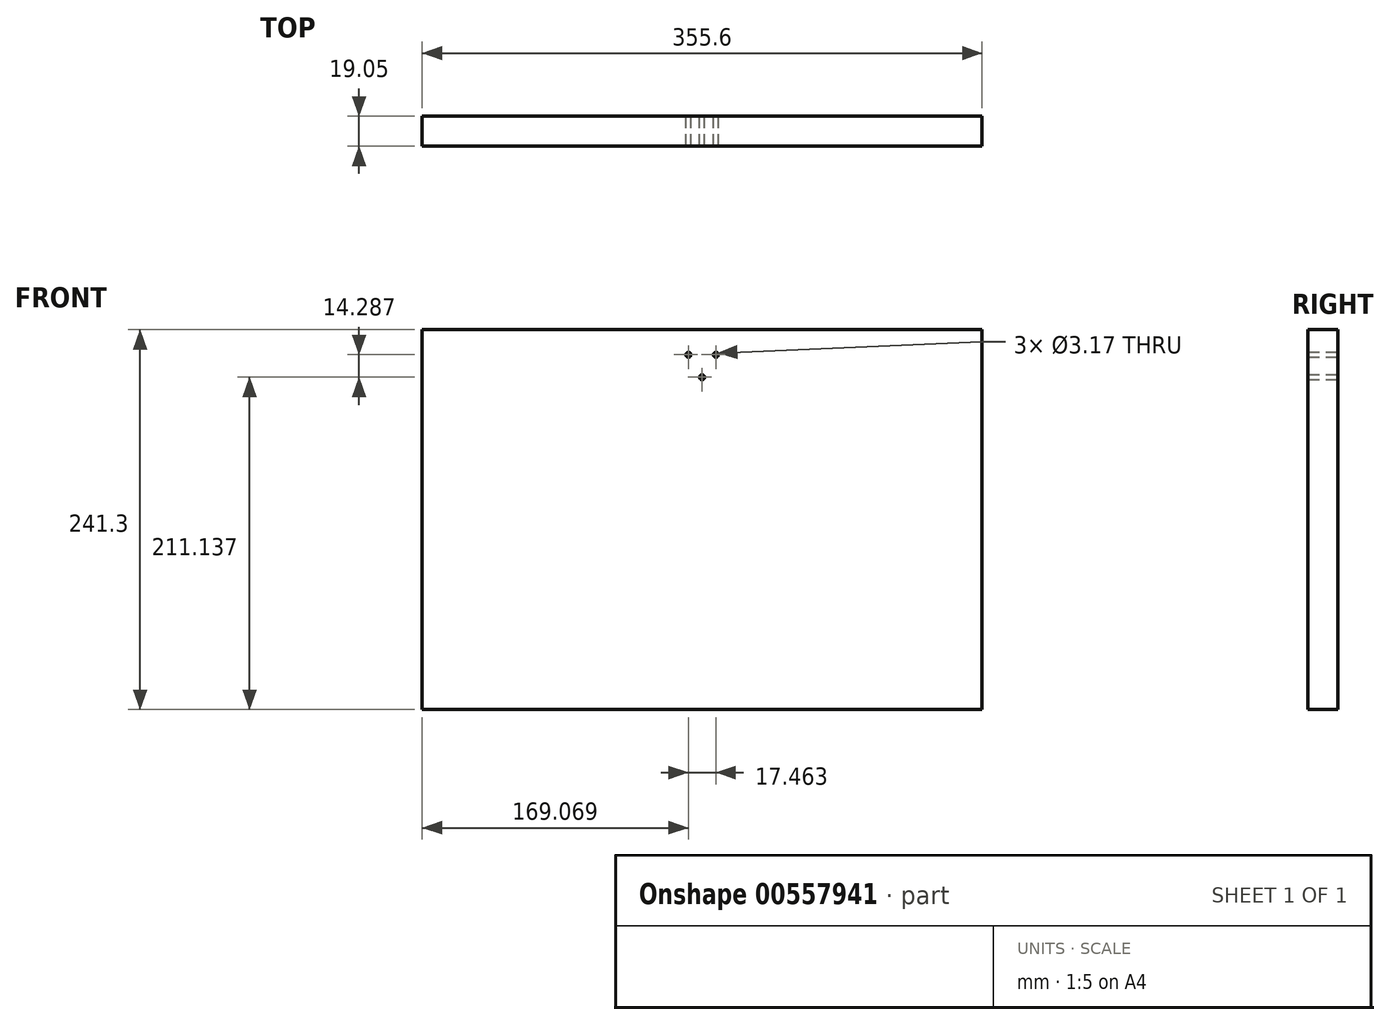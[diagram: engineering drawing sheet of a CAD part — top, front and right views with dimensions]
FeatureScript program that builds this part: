
annotation { "Feature Type Name" : "Feature", "Feature Type Description" : "" }
export const myFeature = defineFeature(function(context is Context, id is Id, definition is map)
    precondition{}
    {
        {
            var Q0;
            Q0=qCreatedBy(makeId("Front.planeOp"),FACE);
            var sketch = newSketch(context, id + "F0", { "sketchPlane" : qUnion([Q0])});
            skLineSegment(sketch, "E0.bottom", {"start": v(381, 21.6) * mm, "end": v(25.4, 21.6) * mm});
            skLineSegment(sketch, "E0.top", {"start": v(381, 262.9) * mm, "end": v(25.4, 262.9) * mm});
            skLineSegment(sketch, "E0.left", {"start": v(381, 21.6) * mm, "end": v(381, 262.9) * mm});
            skLineSegment(sketch, "E0.right", {"start": v(25.4, 21.6) * mm, "end": v(25.4, 262.9) * mm});
            skCircle(sketch, "E1", {"center": v(203.2, 232.73) * mm, "radius": 1.59 * mm});
            skCircle(sketch, "E2", {"center": v(211.93, 247.02) * mm, "radius": 1.59 * mm});
            skCircle(sketch, "E3", {"center": v(194.47, 247.02) * mm, "radius": 1.59 * mm});
            skSolve(sketch);
        }
        {
            var Q0;
            Q0=makeQuery(id+"F0.imprint","IMPRINT",FACE,{"disambiguationData":[TD([[makeQuery(id+"F0.imprint","IMPRINT",EDGE,{"derivedFrom":sQuery(id+"F0.wireOp",EDGE,"E0.bottom")}),-1.0]])]});
            extrude(context, id + "F1", {"entities" : qUnion([Q0]), "depth" : 19.05 * mm, "offsetDistance" : 25.4 * mm});
        }
    });
